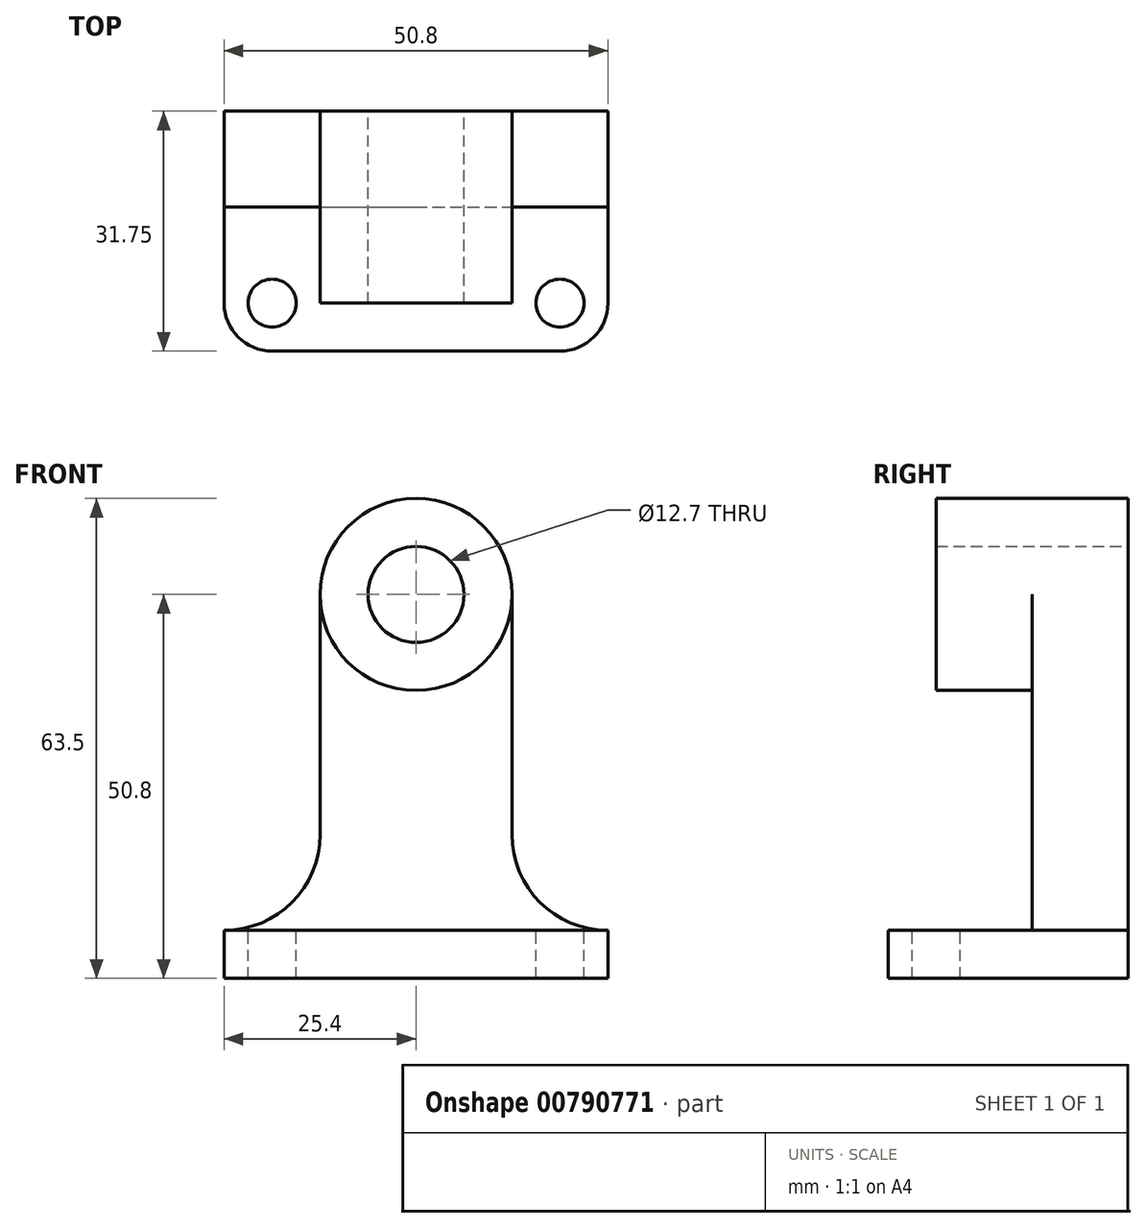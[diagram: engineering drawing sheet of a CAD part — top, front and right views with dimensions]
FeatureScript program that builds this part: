
annotation { "Feature Type Name" : "Feature", "Feature Type Description" : "" }
export const myFeature = defineFeature(function(context is Context, id is Id, definition is map)
    precondition{}
    {
        {
            var Q0;
            Q0=qCreatedBy(makeId("Front.planeOp"),FACE);
            var sketch = newSketch(context, id + "F0", { "sketchPlane" : qUnion([Q0])});
            skLineSegment(sketch, "E0", {"start": v(0, 0) * mm, "end": v(50.8, 0) * mm});
            skLineSegment(sketch, "E1", {"start": v(50.8, 0) * mm, "end": v(50.8, 63.5) * mm});
            skLineSegment(sketch, "E2", {"start": v(50.8, 63.5) * mm, "end": v(0, 63.5) * mm});
            skLineSegment(sketch, "E3", {"start": v(0, 63.5) * mm, "end": v(0, 0) * mm});
            skSolve(sketch);
        }
        {
            var Q0;
            Q0=makeQuery(id+"F0.imprint","IMPRINT",FACE,{"disambiguationData":[TD([[makeQuery(id+"F0.imprint","IMPRINT",EDGE,{"derivedFrom":sQuery(id+"F0.wireOp",EDGE,"E0")}),1.0]])]});
            extrude(context, id + "F1", {"entities" : qUnion([Q0]), "depth" : 31.75 * mm, "offsetDistance" : 25.4 * mm});
        }
        {
            var Q0;
            Q0=makeQuery(id+"F1.opExtrude","CAP_FACE",FACE,{"disambiguationData":[OSD([sQuery(id+"F0.wireOp",EDGE,"E0"),sQuery(id+"F0.wireOp",EDGE,"E1"),sQuery(id+"F0.wireOp",EDGE,"E2"),sQuery(id+"F0.wireOp",EDGE,"E3")])],"isStart":false});
            var sketch = newSketch(context, id + "F2", { "sketchPlane" : qUnion([Q0])});
            skLineSegment(sketch, "E4", {"start": v(0, 6.35) * mm, "end": v(50.8, 6.35) * mm});
            skLineSegment(sketch, "E5", {"start": v(12.7, 6.35) * mm, "end": v(12.7, 63.5) * mm});
            skLineSegment(sketch, "E6", {"start": v(12.7, 63.5) * mm, "end": v(38.1, 63.5) * mm});
            skLineSegment(sketch, "E7", {"start": v(38.1, 63.5) * mm, "end": v(38.1, 6.35) * mm});
            skLineSegment(sketch, "E8", {"start": v(12.7, 38.1) * mm, "end": v(38.1, 38.1) * mm});
            skSolve(sketch);
        }
        {
            var Q0;
            {var subQ4=makeQuery(id+"F1.opExtrude","CAP_EDGE",EDGE,{"disambiguationData":[OSD([sQuery(id+"F0.wireOp",EDGE,"E3")])],"isStart":false});var subQ6=sQuery(id+"F2.wireOp",EDGE,"E4");var subQ7=makeQuery(id+"F2.imprint","INTERSECT",VERTEX,{"derivedFrom":[subQ4,subQ6]});Q0=makeQuery(id+"F2.imprint","IMPRINT",FACE,{"disambiguationData":[TD([[makeQuery(id+"F2.imprint","IMPRINT",EDGE,{"disambiguationData":[TD([[subQ7,-1.0]])],"derivedFrom":subQ6}),1.0]])]});}
            var Q1;
            {var subQ5=sQuery(id+"F2.wireOp",EDGE,"E8");Q1=makeQuery(id+"F2.imprint","IMPRINT",FACE,{"disambiguationData":[TD([[makeQuery(id+"F2.imprint","IMPRINT",EDGE,{"derivedFrom":subQ5}),-1.0]])]});}
            var Q2;
            {var subQ1=makeQuery(id+"F1.opExtrude","CAP_EDGE",EDGE,{"disambiguationData":[OSD([sQuery(id+"F0.wireOp",EDGE,"E1")])],"isStart":false});var subQ3=sQuery(id+"F2.wireOp",EDGE,"E4");var subQ4=makeQuery(id+"F2.imprint","INTERSECT",VERTEX,{"derivedFrom":[subQ1,subQ3]});Q2=makeQuery(id+"F2.imprint","IMPRINT",FACE,{"disambiguationData":[TD([[makeQuery(id+"F2.imprint","IMPRINT",EDGE,{"disambiguationData":[TD([[subQ4,1.0]])],"derivedFrom":subQ3}),1.0]])]});}
            extrude(context, id + "F3", {"entities" : qUnion([Q0, Q1, Q2]), "operationType" : NewBodyOperationType.REMOVE, "oppositeDirection" : true, "depth" : 19.05 * mm, "offsetDistance" : 25.4 * mm});
        }
        {
            var Q0;
            {var subQ0=sQuery(id+"F0.wireOp",EDGE,"E2");Q0=makeQuery(id+"F3.boolean.opBoolean","SPLIT",FACE,{"disambiguationData":[TD([makeQuery(id+"F1.opExtrude","SWEPT_FACE",FACE,{"disambiguationData":[OSD([subQ0])]})])],"derivedFrom":makeQuery(id+"F1.opExtrude","CAP_FACE",FACE,{"disambiguationData":[OSD([sQuery(id+"F0.wireOp",EDGE,"E0"),sQuery(id+"F0.wireOp",EDGE,"E1"),subQ0,sQuery(id+"F0.wireOp",EDGE,"E3")])],"isStart":false})});}
            var sketch = newSketch(context, id + "F4", { "sketchPlane" : qUnion([Q0])});
            skCircle(sketch, "E9", {"center": v(25.4, 50.8) * mm, "radius": 12.7 * mm});
            skPoint(sketch, "E9.centerSnap0", {"position": v(38.1, 50.8) * mm});
            skSolve(sketch);
        }
        {
            var Q0;
            {var subQ0=sQuery(id+"F4.wireOp",EDGE,"E9");var subQ1=makeQuery(id+"F1.opExtrude","CAP_EDGE",EDGE,{"disambiguationData":[OSD([sQuery(id+"F0.wireOp",EDGE,"E2")])],"isStart":false});var subQ2=makeQuery(id+"F4.imprint","INTERSECT",VERTEX,{"derivedFrom":[subQ1,subQ0]});Q0=makeQuery(id+"F4.imprint","IMPRINT",FACE,{"disambiguationData":[TD([[makeQuery(id+"F4.imprint","IMPRINT",EDGE,{"disambiguationData":[TD([[subQ2,-1.0]])],"derivedFrom":subQ0}),-1.0]])]});}
            var Q1;
            {var subQ0=sQuery(id+"F4.wireOp",EDGE,"E9");var subQ1=makeQuery(id+"F1.opExtrude","CAP_EDGE",EDGE,{"disambiguationData":[OSD([sQuery(id+"F0.wireOp",EDGE,"E2")])],"isStart":false});var subQ2=makeQuery(id+"F4.imprint","INTERSECT",VERTEX,{"derivedFrom":[subQ1,subQ0]});Q1=makeQuery(id+"F4.imprint","IMPRINT",FACE,{"disambiguationData":[TD([[makeQuery(id+"F4.imprint","IMPRINT",EDGE,{"disambiguationData":[TD([[subQ2,1.0]])],"derivedFrom":subQ0}),-1.0]])]});}
            var Q2;
            {var subQ0=sQuery(id+"F4.wireOp",EDGE,"E9");var subQ1=makeQuery(id+"F3.boolean.opBoolean","COPY",EDGE,{"derivedFrom":makeQuery(id+"F3.opExtrude","CAP_EDGE",EDGE,{"disambiguationData":[OSD([sQuery(id+"F2.wireOp",EDGE,"E5")])],"isStart":true})});var subQ2=makeQuery(id+"F4.imprint","INTERSECT",VERTEX,{"derivedFrom":[subQ1,subQ0]});Q2=makeQuery(id+"F4.imprint","IMPRINT",FACE,{"disambiguationData":[TD([[makeQuery(id+"F4.imprint","IMPRINT",EDGE,{"disambiguationData":[TD([[subQ2,-1.0]])],"derivedFrom":subQ0}),-1.0]])]});}
            var Q3;
            {var subQ0=sQuery(id+"F4.wireOp",EDGE,"E9");var subQ1=makeQuery(id+"F3.boolean.opBoolean","COPY",EDGE,{"derivedFrom":makeQuery(id+"F3.opExtrude","CAP_EDGE",EDGE,{"disambiguationData":[OSD([sQuery(id+"F2.wireOp",EDGE,"E7")])],"isStart":true})});var subQ2=makeQuery(id+"F4.imprint","INTERSECT",VERTEX,{"derivedFrom":[subQ1,subQ0]});Q3=makeQuery(id+"F4.imprint","IMPRINT",FACE,{"disambiguationData":[TD([[makeQuery(id+"F4.imprint","IMPRINT",EDGE,{"disambiguationData":[TD([[subQ2,1.0]])],"derivedFrom":subQ0}),-1.0]])]});}
            extrude(context, id + "F5", {"entities" : qUnion([Q0, Q1, Q2, Q3]), "operationType" : NewBodyOperationType.REMOVE, "oppositeDirection" : true, "depth" : 19.05 * mm, "offsetDistance" : 25.4 * mm});
        }
        {
            var Q0;
            {var subQ0=sQuery(id+"F0.wireOp",EDGE,"E2");Q0=makeQuery(id+"F3.boolean.opBoolean","SPLIT",FACE,{"disambiguationData":[TD([makeQuery(id+"F1.opExtrude","SWEPT_FACE",FACE,{"disambiguationData":[OSD([subQ0])]})])],"derivedFrom":makeQuery(id+"F1.opExtrude","CAP_FACE",FACE,{"disambiguationData":[OSD([sQuery(id+"F0.wireOp",EDGE,"E0"),sQuery(id+"F0.wireOp",EDGE,"E1"),subQ0,sQuery(id+"F0.wireOp",EDGE,"E3")])],"isStart":false})});}
            extrude(context, id + "F6", {"entities" : qUnion([Q0]), "operationType" : NewBodyOperationType.REMOVE, "oppositeDirection" : true, "depth" : 6.35 * mm, "offsetDistance" : 25.4 * mm});
        }
        {
            var Q0;
            {var subQ0=sQuery(id+"F4.wireOp",EDGE,"E9");var subQ1=sQuery(id+"F2.wireOp",EDGE,"E8");var subQ2=sQuery(id+"F2.wireOp",EDGE,"E7");var subQ3=sQuery(id+"F2.wireOp",EDGE,"E5");var subQ4=sQuery(id+"F0.wireOp",EDGE,"E2");Q0=makeQuery(id+"F5.boolean.opBoolean","MERGE",FACE,{"derivedFrom":[makeQuery(id+"F3.boolean.opBoolean","COPY",FACE,{"derivedFrom":makeQuery(id+"F3.opExtrude","CAP_FACE",FACE,{"disambiguationData":[OSD([sQuery(id+"F0.wireOp",EDGE,"E1"),subQ4,sQuery(id+"F0.wireOp",EDGE,"E3"),sQuery(id+"F2.wireOp",EDGE,"E4"),subQ3,subQ2,subQ1])],"isStart":false})}),makeQuery(id+"F5.opExtrude","CAP_FACE",FACE,{"disambiguationData":[OSD([subQ4,subQ2,subQ0])],"isStart":false}),makeQuery(id+"F5.opExtrude","CAP_FACE",FACE,{"disambiguationData":[OSD([subQ4,subQ3,subQ0])],"isStart":false}),makeQuery(id+"F5.opExtrude","CAP_FACE",FACE,{"disambiguationData":[OSD([subQ3,subQ1,subQ0])],"isStart":false}),makeQuery(id+"F5.opExtrude","CAP_FACE",FACE,{"disambiguationData":[OSD([subQ2,subQ1,subQ0])],"isStart":false})]});}
            var sketch = newSketch(context, id + "F7", { "sketchPlane" : qUnion([Q0])});
            skLineSegment(sketch, "E10", {"start": v(38.1, 63.5) * mm, "end": v(38.1, 6.35) * mm});
            skLineSegment(sketch, "E11", {"start": v(12.7, 63.5) * mm, "end": v(12.7, 6.35) * mm});
            skCircle(sketch, "E12", {"center": v(0, 19.05) * mm, "radius": 12.7 * mm});
            skCircle(sketch, "E13", {"center": v(50.8, 19.05) * mm, "radius": 12.7 * mm});
            skSolve(sketch);
        }
        {
            var Q0;
            {var subQ0=sQuery(id+"F7.wireOp",EDGE,"E12");Q0=makeQuery(id+"F7.imprint","IMPRINT",FACE,{"disambiguationData":[TD([[makeQuery(id+"F7.imprint","IMPRINT",EDGE,{"disambiguationData":[TD([[makeQuery(id+"F7.imprint","INTERSECT",VERTEX,{"derivedFrom":[sQuery(id+"F7.wireOp",EDGE,"E11"),subQ0]}),1.0]])],"derivedFrom":subQ0}),1.0]])]});}
            var Q1;
            {var subQ11=sQuery(id+"F7.wireOp",EDGE,"E12");var subQ12=sQuery(id+"F7.wireOp",EDGE,"E11");Q1=makeQuery(id+"F7.imprint","IMPRINT",FACE,{"disambiguationData":[TD([[makeQuery(id+"F7.imprint","IMPRINT",EDGE,{"disambiguationData":[TD([[makeQuery(id+"F7.imprint","INTERSECT",VERTEX,{"derivedFrom":[subQ12,subQ11]}),1.0]])],"derivedFrom":subQ12}),-1.0]])]});}
            var Q2;
            {var subQ0=sQuery(id+"F7.wireOp",EDGE,"E13");var subQ1=sQuery(id+"F7.wireOp",EDGE,"E10");var subQ2=makeQuery(id+"F7.imprint","INTERSECT",VERTEX,{"derivedFrom":[subQ1,subQ0]});Q2=makeQuery(id+"F7.imprint","IMPRINT",FACE,{"disambiguationData":[TD([[makeQuery(id+"F7.imprint","IMPRINT",EDGE,{"disambiguationData":[TD([[subQ2,1.0]])],"derivedFrom":subQ0}),-1.0]])]});}
            var Q3;
            {var subQ0=sQuery(id+"F7.wireOp",EDGE,"E13");var subQ1=makeQuery(id+"F7.imprint","INTERSECT",VERTEX,{"derivedFrom":[sQuery(id+"F7.wireOp",EDGE,"E10"),subQ0]});Q3=makeQuery(id+"F7.imprint","IMPRINT",FACE,{"disambiguationData":[TD([[makeQuery(id+"F7.imprint","IMPRINT",EDGE,{"disambiguationData":[TD([[subQ1,1.0]])],"derivedFrom":subQ0}),1.0]])]});}
            extrude(context, id + "F8", {"entities" : qUnion([Q0, Q1, Q2, Q3]), "operationType" : NewBodyOperationType.REMOVE, "oppositeDirection" : true, "depth" : 25.4 * mm, "offsetDistance" : 25.4 * mm});
        }
        {
            var Q0;
            {var subQ0=sQuery(id+"F0.wireOp",EDGE,"E2");var subQ1=sQuery(id+"F4.wireOp",EDGE,"E9");var subQ2=sQuery(id+"F2.wireOp",EDGE,"E8");var subQ3=makeQuery(id+"F4.imprint","INTERSECT",VERTEX,{"derivedFrom":[makeQuery(id+"F3.boolean.opBoolean","COPY",EDGE,{"derivedFrom":makeQuery(id+"F3.opExtrude","CAP_EDGE",EDGE,{"disambiguationData":[OSD([subQ2])],"isStart":true})}),subQ1]});var subQ4=sQuery(id+"F2.wireOp",EDGE,"E5");var subQ6=makeQuery(id+"F4.imprint","INTERSECT",VERTEX,{"derivedFrom":[makeQuery(id+"F1.opExtrude","CAP_EDGE",EDGE,{"disambiguationData":[OSD([subQ0])],"isStart":false}),subQ1]});var subQ7=sQuery(id+"F2.wireOp",EDGE,"E7");var subQ8=makeQuery(id+"F4.imprint","INTERSECT",VERTEX,{"derivedFrom":[makeQuery(id+"F3.boolean.opBoolean","COPY",EDGE,{"derivedFrom":makeQuery(id+"F3.opExtrude","CAP_EDGE",EDGE,{"disambiguationData":[OSD([subQ7])],"isStart":true})}),subQ1]});var subQ9=makeQuery(id+"F3.boolean.opBoolean","COPY",FACE,{"derivedFrom":makeQuery(id+"F3.opExtrude","CAP_FACE",FACE,{"disambiguationData":[OSD([sQuery(id+"F0.wireOp",EDGE,"E1"),subQ0,sQuery(id+"F0.wireOp",EDGE,"E3"),sQuery(id+"F2.wireOp",EDGE,"E4"),subQ4,subQ7,subQ2])],"isStart":false})});Q0=makeQuery(id+"F8.boolean.opBoolean","SPLIT",FACE,{"disambiguationData":[TD([makeQuery(id+"F1.opExtrude","SWEPT_FACE",FACE,{"disambiguationData":[OSD([subQ0])]}),subQ9,makeQuery(id+"F5.boolean.opBoolean","MERGE",FACE,{"derivedFrom":[],"fromTools":[makeQuery(id+"F5.opExtrude","SWEPT_FACE",FACE,{"disambiguationData":[OSD([subQ1]),TDD([makeQuery(id+"F4.imprint","IMPRINT",EDGE,{"disambiguationData":[TD([[subQ8,1.0]])],"derivedFrom":subQ1})])]}),makeQuery(id+"F5.opExtrude","SWEPT_FACE",FACE,{"disambiguationData":[OSD([subQ1]),TDD([makeQuery(id+"F4.imprint","IMPRINT",EDGE,{"disambiguationData":[TD([[subQ8,-1.0]])],"derivedFrom":subQ1})])]}),makeQuery(id+"F5.opExtrude","SWEPT_FACE",FACE,{"disambiguationData":[OSD([subQ1]),TDD([makeQuery(id+"F4.imprint","IMPRINT",EDGE,{"disambiguationData":[TD([[subQ6,-1.0]])],"derivedFrom":subQ1})])]}),makeQuery(id+"F5.opExtrude","SWEPT_FACE",FACE,{"disambiguationData":[OSD([subQ1]),TDD([makeQuery(id+"F4.imprint","IMPRINT",EDGE,{"disambiguationData":[TD([[subQ3,1.0]])],"derivedFrom":subQ1})])]})]}),makeQuery(id+"F8.opExtrude","SWEPT_FACE",FACE,{"disambiguationData":[OSD([sQuery(id+"F7.wireOp",EDGE,"E11")])]})])],"derivedFrom":makeQuery(id+"F5.boolean.opBoolean","MERGE",FACE,{"derivedFrom":[subQ9],"fromTools":[makeQuery(id+"F5.opExtrude","CAP_FACE",FACE,{"disambiguationData":[OSD([subQ7,subQ2,subQ1])],"isStart":false}),makeQuery(id+"F5.opExtrude","CAP_FACE",FACE,{"disambiguationData":[OSD([subQ0,subQ7,subQ1])],"isStart":false}),makeQuery(id+"F5.opExtrude","CAP_FACE",FACE,{"disambiguationData":[OSD([subQ0,subQ4,subQ1])],"isStart":false}),makeQuery(id+"F5.opExtrude","CAP_FACE",FACE,{"disambiguationData":[OSD([subQ4,subQ2,subQ1])],"isStart":false})]})});}
            var Q1;
            {var subQ0=sQuery(id+"F0.wireOp",EDGE,"E2");var subQ1=sQuery(id+"F4.wireOp",EDGE,"E9");var subQ2=sQuery(id+"F2.wireOp",EDGE,"E8");var subQ3=makeQuery(id+"F4.imprint","INTERSECT",VERTEX,{"derivedFrom":[makeQuery(id+"F3.boolean.opBoolean","COPY",EDGE,{"derivedFrom":makeQuery(id+"F3.opExtrude","CAP_EDGE",EDGE,{"disambiguationData":[OSD([subQ2])],"isStart":true})}),subQ1]});var subQ4=sQuery(id+"F2.wireOp",EDGE,"E5");var subQ6=makeQuery(id+"F4.imprint","INTERSECT",VERTEX,{"derivedFrom":[makeQuery(id+"F1.opExtrude","CAP_EDGE",EDGE,{"disambiguationData":[OSD([subQ0])],"isStart":false}),subQ1]});var subQ7=sQuery(id+"F2.wireOp",EDGE,"E7");var subQ8=makeQuery(id+"F4.imprint","INTERSECT",VERTEX,{"derivedFrom":[makeQuery(id+"F3.boolean.opBoolean","COPY",EDGE,{"derivedFrom":makeQuery(id+"F3.opExtrude","CAP_EDGE",EDGE,{"disambiguationData":[OSD([subQ7])],"isStart":true})}),subQ1]});var subQ9=makeQuery(id+"F3.boolean.opBoolean","COPY",FACE,{"derivedFrom":makeQuery(id+"F3.opExtrude","CAP_FACE",FACE,{"disambiguationData":[OSD([sQuery(id+"F0.wireOp",EDGE,"E1"),subQ0,sQuery(id+"F0.wireOp",EDGE,"E3"),sQuery(id+"F2.wireOp",EDGE,"E4"),subQ4,subQ7,subQ2])],"isStart":false})});Q1=makeQuery(id+"F8.boolean.opBoolean","SPLIT",FACE,{"disambiguationData":[TD([makeQuery(id+"F1.opExtrude","SWEPT_FACE",FACE,{"disambiguationData":[OSD([subQ0])]}),subQ9,makeQuery(id+"F5.boolean.opBoolean","MERGE",FACE,{"derivedFrom":[],"fromTools":[makeQuery(id+"F5.opExtrude","SWEPT_FACE",FACE,{"disambiguationData":[OSD([subQ1]),TDD([makeQuery(id+"F4.imprint","IMPRINT",EDGE,{"disambiguationData":[TD([[subQ8,1.0]])],"derivedFrom":subQ1})])]}),makeQuery(id+"F5.opExtrude","SWEPT_FACE",FACE,{"disambiguationData":[OSD([subQ1]),TDD([makeQuery(id+"F4.imprint","IMPRINT",EDGE,{"disambiguationData":[TD([[subQ8,-1.0]])],"derivedFrom":subQ1})])]}),makeQuery(id+"F5.opExtrude","SWEPT_FACE",FACE,{"disambiguationData":[OSD([subQ1]),TDD([makeQuery(id+"F4.imprint","IMPRINT",EDGE,{"disambiguationData":[TD([[subQ6,-1.0]])],"derivedFrom":subQ1})])]}),makeQuery(id+"F5.opExtrude","SWEPT_FACE",FACE,{"disambiguationData":[OSD([subQ1]),TDD([makeQuery(id+"F4.imprint","IMPRINT",EDGE,{"disambiguationData":[TD([[subQ3,1.0]])],"derivedFrom":subQ1})])]})]}),makeQuery(id+"F8.opExtrude","SWEPT_FACE",FACE,{"disambiguationData":[OSD([sQuery(id+"F7.wireOp",EDGE,"E10")])]})])],"derivedFrom":makeQuery(id+"F5.boolean.opBoolean","MERGE",FACE,{"derivedFrom":[subQ9],"fromTools":[makeQuery(id+"F5.opExtrude","CAP_FACE",FACE,{"disambiguationData":[OSD([subQ7,subQ2,subQ1])],"isStart":false}),makeQuery(id+"F5.opExtrude","CAP_FACE",FACE,{"disambiguationData":[OSD([subQ0,subQ7,subQ1])],"isStart":false}),makeQuery(id+"F5.opExtrude","CAP_FACE",FACE,{"disambiguationData":[OSD([subQ0,subQ4,subQ1])],"isStart":false}),makeQuery(id+"F5.opExtrude","CAP_FACE",FACE,{"disambiguationData":[OSD([subQ4,subQ2,subQ1])],"isStart":false})]})});}
            var Q2;
            Q2 = qSketchRegion(id + "F10", true);
            extrude(context, id + "F9", {"entities" : qUnion([Q0, Q1, Q2]), "operationType" : NewBodyOperationType.REMOVE, "oppositeDirection" : true, "depth" : 25.4 * mm, "offsetDistance" : 25.4 * mm});
        }
        {
            var Q0;
            Q0=makeQuery(id+"F3.boolean.opBoolean","COPY",FACE,{"derivedFrom":makeQuery(id+"F3.opExtrude","SWEPT_FACE",FACE,{"disambiguationData":[OSD([sQuery(id+"F2.wireOp",EDGE,"E4")])]})});
            var sketch = newSketch(context, id + "F10", { "sketchPlane" : qUnion([Q0])});
            skCircle(sketch, "E14", {"center": v(44.45, -25.4) * mm, "radius": 6.35 * mm});
            skCircle(sketch, "E15", {"center": v(6.35, -25.4) * mm, "radius": 6.35 * mm});
            skSolve(sketch);
        }
        {
            var Q0;
            {var subQ0=sQuery(id+"F10.wireOp",EDGE,"E15");var subQ1=sQuery(id+"F2.wireOp",EDGE,"E4");var subQ4=makeQuery(id+"F3.boolean.opBoolean","COPY",EDGE,{"derivedFrom":makeQuery(id+"F3.opExtrude","CAP_EDGE",EDGE,{"disambiguationData":[OSD([subQ1])],"isStart":true})});var subQ5=makeQuery(id+"F10.imprint","INTERSECT",VERTEX,{"derivedFrom":[subQ4,subQ0]});Q0=makeQuery(id+"F10.imprint","IMPRINT",FACE,{"disambiguationData":[TD([[makeQuery(id+"F10.imprint","IMPRINT",EDGE,{"disambiguationData":[TD([[subQ5,1.0]])],"derivedFrom":subQ0}),-1.0]])]});}
            var Q1;
            {var subQ0=sQuery(id+"F10.wireOp",EDGE,"E14");var subQ1=sQuery(id+"F2.wireOp",EDGE,"E4");var subQ4=makeQuery(id+"F3.boolean.opBoolean","COPY",EDGE,{"derivedFrom":makeQuery(id+"F3.opExtrude","CAP_EDGE",EDGE,{"disambiguationData":[OSD([subQ1])],"isStart":true})});var subQ5=makeQuery(id+"F10.imprint","INTERSECT",VERTEX,{"derivedFrom":[subQ4,subQ0]});Q1=makeQuery(id+"F10.imprint","IMPRINT",FACE,{"disambiguationData":[TD([[makeQuery(id+"F10.imprint","IMPRINT",EDGE,{"disambiguationData":[TD([[subQ5,-1.0]])],"derivedFrom":subQ0}),-1.0]])]});}
            extrude(context, id + "F11", {"entities" : qUnion([Q0, Q1]), "operationType" : NewBodyOperationType.REMOVE, "oppositeDirection" : true, "depth" : 6.35 * mm, "offsetDistance" : 25.4 * mm});
        }
        {
            var Q0;
            Q0=makeQuery(id+"F3.boolean.opBoolean","COPY",FACE,{"derivedFrom":makeQuery(id+"F3.opExtrude","SWEPT_FACE",FACE,{"disambiguationData":[OSD([sQuery(id+"F2.wireOp",EDGE,"E4")])]})});
            var sketch = newSketch(context, id + "F12", { "sketchPlane" : qUnion([Q0])});
            skCircle(sketch, "E16", {"center": v(44.45, -25.4) * mm, "radius": 3.18 * mm});
            skCircle(sketch, "E17", {"center": v(6.35, -25.4) * mm, "radius": 3.18 * mm});
            skSolve(sketch);
        }
        {
            var Q0;
            Q0=makeQuery(id+"F12.imprint","IMPRINT",FACE,{"disambiguationData":[TD([[makeQuery(id+"F12.imprint","IMPRINT",EDGE,{"derivedFrom":sQuery(id+"F12.wireOp",EDGE,"E17")}),1.0]])]});
            var Q1;
            Q1=makeQuery(id+"F12.imprint","IMPRINT",FACE,{"disambiguationData":[TD([[makeQuery(id+"F12.imprint","IMPRINT",EDGE,{"derivedFrom":sQuery(id+"F12.wireOp",EDGE,"E16")}),1.0]])]});
            extrude(context, id + "F13", {"entities" : qUnion([Q0, Q1]), "operationType" : NewBodyOperationType.REMOVE, "oppositeDirection" : true, "depth" : 6.35 * mm});
        }
        {
            var Q0;
            Q0=makeQuery(id+"F1.opExtrude","CAP_FACE",FACE,{"disambiguationData":[OSD([sQuery(id+"F0.wireOp",EDGE,"E0"),sQuery(id+"F0.wireOp",EDGE,"E1"),sQuery(id+"F0.wireOp",EDGE,"E2"),sQuery(id+"F0.wireOp",EDGE,"E3")])],"isStart":true});
            var sketch = newSketch(context, id + "F14", { "sketchPlane" : qUnion([Q0])});
            skCircle(sketch, "E18", {"center": v(-25.4, 50.8) * mm, "radius": 6.35 * mm});
            skSolve(sketch);
        }
        {
            var Q0;
            Q0=makeQuery(id+"F14.imprint","IMPRINT",FACE,{"disambiguationData":[TD([[makeQuery(id+"F14.imprint","IMPRINT",EDGE,{"derivedFrom":sQuery(id+"F14.wireOp",EDGE,"E18")}),1.0]])]});
            extrude(context, id + "F15", {"entities" : qUnion([Q0]), "operationType" : NewBodyOperationType.REMOVE, "oppositeDirection" : true, "depth" : 25.4 * mm, "offsetDistance" : 25.4 * mm});
        }
    });
